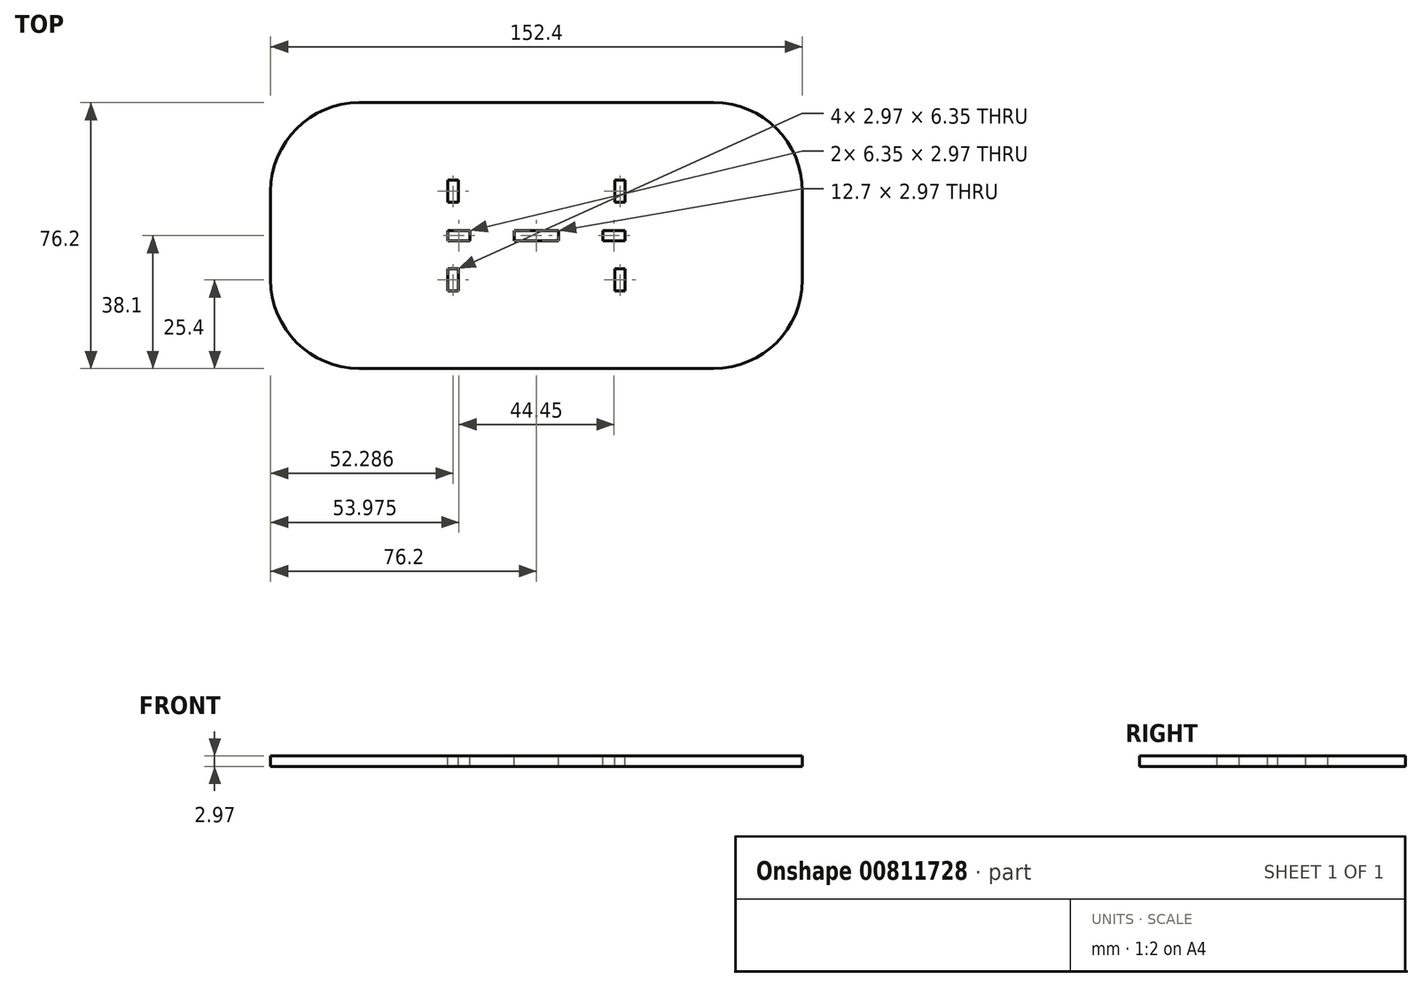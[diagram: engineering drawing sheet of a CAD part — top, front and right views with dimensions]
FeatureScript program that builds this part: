
annotation { "Feature Type Name" : "Feature", "Feature Type Description" : "" }
export const myFeature = defineFeature(function(context is Context, id is Id, definition is map)
    precondition{}
    {
        {
            var Q0;
            Q0=qCreatedBy(makeId("Top.planeOp"),FACE);
            var sketch = newSketch(context, id + "F0", { "sketchPlane" : qUnion([Q0])});
            skLineSegment(sketch, "E0.bottom", {"start": v(76.2, 38.1) * mm, "end": v(-76.2, 38.1) * mm});
            skLineSegment(sketch, "E0.top", {"start": v(76.2, -38.1) * mm, "end": v(-76.2, -38.1) * mm});
            skLineSegment(sketch, "E0.left", {"start": v(76.2, 38.1) * mm, "end": v(76.2, -38.1) * mm});
            skLineSegment(sketch, "E0.right", {"start": v(-76.2, 38.1) * mm, "end": v(-76.2, -38.1) * mm});
            skPoint(sketch, "E0.middle", {"position": v(0, 0) * mm});
            skSolve(sketch);
        }
        {
            var Q0;
            Q0 = qSketchRegion(id + "F0", true);
            extrude(context, id + "F1", {"entities" : qUnion([Q0]), "depth" : 2.97 * mm, "offsetDistance" : 25.4 * mm});
        }
        {
            var Q0;
            Q0=makeQuery(id+"F1.opExtrude","SWEPT_EDGE",EDGE,{"disambiguationData":[OSD([sQuery(id+"F0.wireOp",EDGE,"E0.top"),sQuery(id+"F0.wireOp",EDGE,"E0.right")])]});
            var Q1;
            Q1=makeQuery(id+"F1.opExtrude","SWEPT_EDGE",EDGE,{"disambiguationData":[OSD([sQuery(id+"F0.wireOp",EDGE,"E0.top"),sQuery(id+"F0.wireOp",EDGE,"E0.left")])]});
            var Q2;
            Q2=makeQuery(id+"F1.opExtrude","SWEPT_EDGE",EDGE,{"disambiguationData":[OSD([sQuery(id+"F0.wireOp",EDGE,"E0.bottom"),sQuery(id+"F0.wireOp",EDGE,"E0.left")])]});
            var Q3;
            Q3=makeQuery(id+"F1.opExtrude","SWEPT_EDGE",EDGE,{"disambiguationData":[OSD([sQuery(id+"F0.wireOp",EDGE,"E0.bottom"),sQuery(id+"F0.wireOp",EDGE,"E0.right")])]});
            fillet(context, id + "F2", {"entities" : qUnion([Q0, Q1, Q2, Q3]), "radius" : 25.4 * mm, "tangentPropagation" : true, "allowEdgeOverflow" : false});
        }
        {
            var Q0;
            Q0=makeQuery(id+"F1.opExtrude","CAP_FACE",FACE,{"disambiguationData":[OSD([sQuery(id+"F0.wireOp",EDGE,"E0.bottom"),sQuery(id+"F0.wireOp",EDGE,"E0.top"),sQuery(id+"F0.wireOp",EDGE,"E0.left"),sQuery(id+"F0.wireOp",EDGE,"E0.right")])],"isStart":false});
            var sketch = newSketch(context, id + "F3", { "sketchPlane" : qUnion([Q0])});
            skLineSegment(sketch, "E1.bottom", {"start": v(6.35, 1.49) * mm, "end": v(-6.35, 1.49) * mm});
            skLineSegment(sketch, "E1.top", {"start": v(6.35, -1.49) * mm, "end": v(-6.35, -1.49) * mm});
            skLineSegment(sketch, "E1.left", {"start": v(6.35, 1.49) * mm, "end": v(6.35, -1.49) * mm});
            skLineSegment(sketch, "E1.right", {"start": v(-6.35, 1.49) * mm, "end": v(-6.35, -1.49) * mm});
            skPoint(sketch, "E1.middle", {"position": v(0, 0) * mm});
            skLineSegment(sketch, "E2.bottom", {"start": v(25.4, 1.49) * mm, "end": v(19.05, 1.49) * mm});
            skLineSegment(sketch, "E2.top", {"start": v(25.4, -1.49) * mm, "end": v(19.05, -1.49) * mm});
            skLineSegment(sketch, "E2.left", {"start": v(25.4, 1.49) * mm, "end": v(25.4, -1.49) * mm});
            skLineSegment(sketch, "E2.right", {"start": v(19.05, 1.49) * mm, "end": v(19.05, -1.49) * mm});
            skPoint(sketch, "E2.middle", {"position": v(22.23, 0) * mm});
            skLineSegment(sketch, "E3.bottom", {"start": v(-19.05, 1.49) * mm, "end": v(-25.4, 1.49) * mm});
            skLineSegment(sketch, "E3.top", {"start": v(-19.05, -1.49) * mm, "end": v(-25.4, -1.49) * mm});
            skLineSegment(sketch, "E3.left", {"start": v(-19.05, 1.49) * mm, "end": v(-19.05, -1.49) * mm});
            skLineSegment(sketch, "E3.right", {"start": v(-25.4, 1.49) * mm, "end": v(-25.4, -1.49) * mm});
            skPoint(sketch, "E3.middle", {"position": v(-22.23, 0) * mm});
            skSolve(sketch);
        }
        {
            var Q0;
            Q0 = qSketchRegion(id + "F3", true);
            extrude(context, id + "F4", {"entities" : qUnion([Q0]), "operationType" : NewBodyOperationType.REMOVE, "oppositeDirection" : true, "depth" : 25.4 * mm, "offsetDistance" : 25.4 * mm});
        }
        {
            var Q0;
            Q0=makeQuery(id+"F1.opExtrude","CAP_FACE",FACE,{"disambiguationData":[OSD([sQuery(id+"F0.wireOp",EDGE,"E0.bottom"),sQuery(id+"F0.wireOp",EDGE,"E0.top"),sQuery(id+"F0.wireOp",EDGE,"E0.left"),sQuery(id+"F0.wireOp",EDGE,"E0.right")])],"isStart":false});
            var sketch = newSketch(context, id + "F5", { "sketchPlane" : qUnion([Q0])});
            skLineSegment(sketch, "E4.bottom", {"start": v(25.4, 9.53) * mm, "end": v(22.43, 9.52) * mm});
            skLineSegment(sketch, "E4.top", {"start": v(25.4, 15.88) * mm, "end": v(22.43, 15.88) * mm});
            skLineSegment(sketch, "E4.left", {"start": v(25.4, 9.53) * mm, "end": v(25.4, 15.88) * mm});
            skLineSegment(sketch, "E4.right", {"start": v(22.43, 9.52) * mm, "end": v(22.43, 15.88) * mm});
            skLineSegment(sketch, "E5.bottom", {"start": v(25.4, -9.53) * mm, "end": v(22.43, -9.53) * mm});
            skLineSegment(sketch, "E5.top", {"start": v(25.4, -15.87) * mm, "end": v(22.43, -15.87) * mm});
            skLineSegment(sketch, "E5.left", {"start": v(25.4, -9.53) * mm, "end": v(25.4, -15.87) * mm});
            skLineSegment(sketch, "E5.right", {"start": v(22.43, -9.53) * mm, "end": v(22.43, -15.87) * mm});
            skLineSegment(sketch, "E6.bottom", {"start": v(-25.4, 9.53) * mm, "end": v(-22.43, 9.53) * mm});
            skLineSegment(sketch, "E6.top", {"start": v(-25.4, 15.88) * mm, "end": v(-22.43, 15.88) * mm});
            skLineSegment(sketch, "E6.left", {"start": v(-25.4, 9.53) * mm, "end": v(-25.4, 15.88) * mm});
            skLineSegment(sketch, "E6.right", {"start": v(-22.43, 9.53) * mm, "end": v(-22.43, 15.88) * mm});
            skLineSegment(sketch, "E7.bottom", {"start": v(-25.4, -9.53) * mm, "end": v(-22.43, -9.53) * mm});
            skLineSegment(sketch, "E7.top", {"start": v(-25.4, -15.88) * mm, "end": v(-22.43, -15.88) * mm});
            skLineSegment(sketch, "E7.left", {"start": v(-25.4, -9.53) * mm, "end": v(-25.4, -15.88) * mm});
            skLineSegment(sketch, "E7.right", {"start": v(-22.43, -9.53) * mm, "end": v(-22.43, -15.88) * mm});
            skSolve(sketch);
        }
        {
            var Q0;
            Q0 = qSketchRegion(id + "F5", true);
            extrude(context, id + "F6", {"entities" : qUnion([Q0]), "operationType" : NewBodyOperationType.REMOVE, "oppositeDirection" : true, "depth" : 25.4 * mm, "offsetDistance" : 25.4 * mm});
        }
    });
